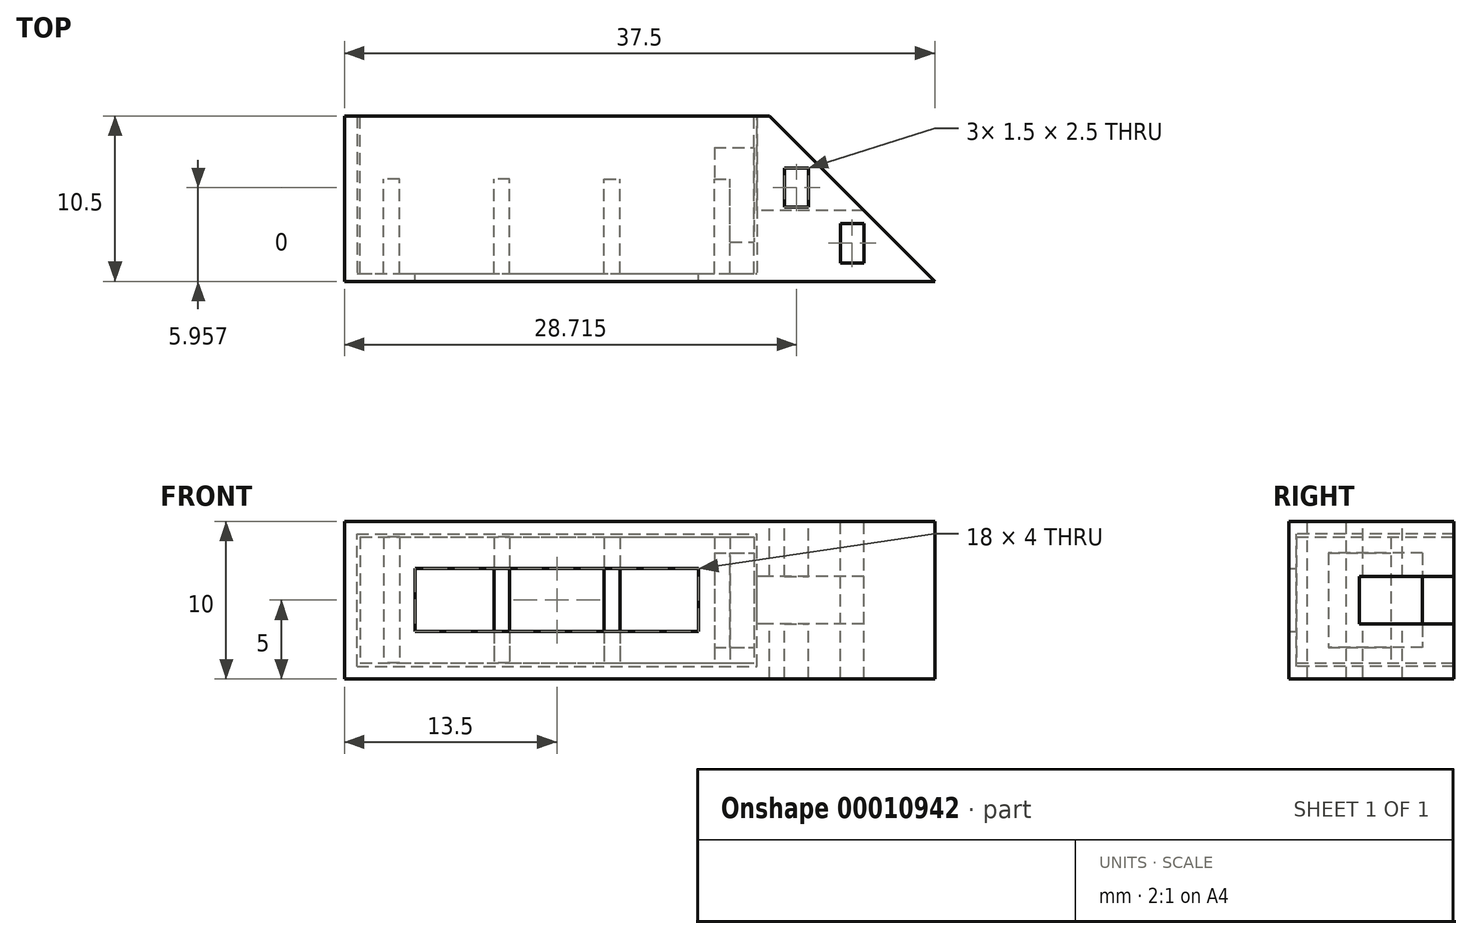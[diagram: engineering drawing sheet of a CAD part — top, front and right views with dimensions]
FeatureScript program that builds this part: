
annotation { "Feature Type Name" : "Feature", "Feature Type Description" : "" }
export const myFeature = defineFeature(function(context is Context, id is Id, definition is map)
    precondition{}
    {
        {
            var Q0;
            Q0=qCreatedBy(makeId("Top.planeOp"),FACE);
            var sketch = newSketch(context, id + "F0", { "sketchPlane" : qUnion([Q0])});
            skLineSegment(sketch, "E0.rect.bottom", {"start": v(-12.5, -5) * mm, "end": v(12.5, -5) * mm});
            skLineSegment(sketch, "E0.rect.top", {"start": v(-12.5, 5) * mm, "end": v(12.5, 5) * mm});
            skLineSegment(sketch, "E0.rect.left", {"start": v(-12.5, -5) * mm, "end": v(-12.5, 5) * mm});
            skLineSegment(sketch, "E0.rect.right", {"start": v(12.5, -5) * mm, "end": v(12.5, 5) * mm});
            skPoint(sketch, "E0.rect.middle", {"position": v(0, 0) * mm});
            skLineSegment(sketch, "E1.bottom", {"start": v(-3, -5) * mm, "end": v(-4, -5) * mm});
            skLineSegment(sketch, "E1.top", {"start": v(-3, 1) * mm, "end": v(-4, 1) * mm});
            skLineSegment(sketch, "E1.left", {"start": v(-3, -5) * mm, "end": v(-3, 1) * mm});
            skLineSegment(sketch, "E1.right", {"start": v(-4, -5) * mm, "end": v(-4, 1) * mm});
            skLineSegment(sketch, "E2.0.MirrorCS", {"start": v(3, -5) * mm, "end": v(3, 1) * mm});
            skLineSegment(sketch, "E3.0.MirrorCS", {"start": v(3, 1) * mm, "end": v(4, 1) * mm});
            skLineSegment(sketch, "E4.0.MirrorCS", {"start": v(4, -5) * mm, "end": v(4, 1) * mm});
            skLineSegment(sketch, "E5", {"start": v(-3.5, 1) * mm, "end": v(-3.5, -6.52) * mm, "construction": true});
            skLineSegment(sketch, "E6.0.MirrorCS", {"start": v(-10, -5) * mm, "end": v(-10, 1) * mm});
            skLineSegment(sketch, "E7.0.MirrorCS", {"start": v(-10, 1) * mm, "end": v(-11, 1) * mm});
            skLineSegment(sketch, "E8.0.MirrorCS", {"start": v(-11, -5) * mm, "end": v(-11, 1) * mm});
            skLineSegment(sketch, "E9", {"start": v(3.5, 1) * mm, "end": v(3.5, -5) * mm, "construction": true});
            skLineSegment(sketch, "E10.0.MirrorCS", {"start": v(11, -5) * mm, "end": v(11, 1) * mm});
            skLineSegment(sketch, "E11.0.MirrorCS", {"start": v(10, -5) * mm, "end": v(10, 1) * mm});
            skLineSegment(sketch, "E12.0.MirrorCS", {"start": v(10, 1) * mm, "end": v(11, 1) * mm});
            skSolve(sketch);
        }
        {
            var Q0;
            Q0=makeQuery(id+"F0.imprint","IMPRINT",FACE,{"disambiguationData":[TD([[makeQuery(id+"F0.imprint","IMPRINT",EDGE,{"derivedFrom":sQuery(id+"F0.wireOp",EDGE,"E0.rect.top")}),-1.0]])]});
            extrude(context, id + "F1", {"entities" : qUnion([Q0]), "depth" : 8 * mm});
        }
        {
            var Q0;
            Q0=makeQuery(id+"F1.opExtrude","SWEPT_FACE",FACE,{"disambiguationData":[OSD([sQuery(id+"F0.wireOp",EDGE,"E0.rect.right")])]});
            var sketch = newSketch(context, id + "F2", { "sketchPlane" : qUnion([Q0])});
            skLineSegment(sketch, "E13", {"start": v(5, 4) * mm, "end": v(-5, 4) * mm, "construction": true});
            skLineSegment(sketch, "E14", {"start": v(0, 8) * mm, "end": v(0, 0) * mm, "construction": true});
            skLineSegment(sketch, "E15.rect.bottom", {"start": v(3, 7) * mm, "end": v(-3, 7) * mm});
            skLineSegment(sketch, "E15.rect.top", {"start": v(3, 1) * mm, "end": v(-3, 1) * mm});
            skLineSegment(sketch, "E15.rect.left", {"start": v(3, 7) * mm, "end": v(3, 1) * mm});
            skLineSegment(sketch, "E15.rect.right", {"start": v(-3, 7) * mm, "end": v(-3, 1) * mm});
            skPoint(sketch, "E15.rect.middle", {"position": v(0, 4) * mm});
            skSolve(sketch);
        }
        {
            var Q0;
            Q0=makeQuery(id+"F2.imprint","IMPRINT",FACE,{"disambiguationData":[TD([[makeQuery(id+"F2.imprint","IMPRINT",EDGE,{"derivedFrom":sQuery(id+"F2.wireOp",EDGE,"E15.rect.bottom")}),1.0]])]});
            extrude(context, id + "F3", {"entities" : qUnion([Q0]), "operationType" : NewBodyOperationType.REMOVE, "oppositeDirection" : true, "depth" : 2.5 * mm});
        }
        {
            var Q0;
            {var subQ0=sQuery(id+"F0.wireOp",EDGE,"E0.rect.bottom");Q0=makeQuery(id+"F1.opExtrude","SWEPT_FACE",FACE,{"disambiguationData":[OSD([subQ0]),TDD([makeQuery(id+"F0.imprint","IMPRINT",EDGE,{"disambiguationData":[TD([[makeQuery(id+"F0.imprint","INTERSECT",VERTEX,{"derivedFrom":[subQ0,sQuery(id+"F0.wireOp",EDGE,"E2.0.MirrorCS")]}),1.0]])],"derivedFrom":subQ0})])]});}
            var sketch = newSketch(context, id + "F4", { "sketchPlane" : qUnion([Q0])});
            skLineSegment(sketch, "E16", {"start": v(0, 0) * mm, "end": v(0, 8) * mm, "construction": true});
            skLineSegment(sketch, "E17", {"start": v(0, 8) * mm, "end": v(0, 4) * mm, "construction": true});
            skLineSegment(sketch, "E18", {"start": v(0, 4) * mm, "end": v(-12.53, 4) * mm, "construction": true});
            skLineSegment(sketch, "E19.rect.bottom", {"start": v(-13.5, -1) * mm, "end": v(13.5, -1) * mm});
            skLineSegment(sketch, "E19.rect.top", {"start": v(-13.5, 9) * mm, "end": v(13.5, 9) * mm});
            skLineSegment(sketch, "E19.rect.left", {"start": v(-13.5, -1) * mm, "end": v(-13.5, 9) * mm});
            skLineSegment(sketch, "E19.rect.right", {"start": v(13.5, -1) * mm, "end": v(13.5, 9) * mm});
            skPoint(sketch, "E19.rect.middle", {"position": v(0, 4) * mm});
            skLineSegment(sketch, "E20.rect.bottom", {"start": v(-9, 2) * mm, "end": v(9, 2) * mm});
            skLineSegment(sketch, "E20.rect.top", {"start": v(-9, 6) * mm, "end": v(9, 6) * mm});
            skLineSegment(sketch, "E20.rect.left", {"start": v(-9, 2) * mm, "end": v(-9, 6) * mm});
            skLineSegment(sketch, "E20.rect.right", {"start": v(9, 2) * mm, "end": v(9, 6) * mm});
            skLineSegment(sketch, "E21.rect.bottom", {"start": v(-12.7, -0.2) * mm, "end": v(12.7, -0.2) * mm});
            skLineSegment(sketch, "E21.rect.top", {"start": v(-12.7, 8.2) * mm, "end": v(12.7, 8.2) * mm});
            skLineSegment(sketch, "E21.rect.left", {"start": v(-12.7, -0.2) * mm, "end": v(-12.7, 8.2) * mm});
            skLineSegment(sketch, "E21.rect.right", {"start": v(12.7, -0.2) * mm, "end": v(12.7, 8.2) * mm});
            skSolve(sketch);
        }
        {
            var Q0;
            Q0 = qSketchRegion(id + "F4", true);
            var Q1;
            {var subQ16=sQuery(id+"F4.wireOp",EDGE,"E20.rect.left");Q1=makeQuery(id+"F4.imprint","IMPRINT",FACE,{"disambiguationData":[TD([[makeQuery(id+"F4.imprint","IMPRINT",EDGE,{"derivedFrom":subQ16}),1.0]])]});}
            var Q2;
            {var subQ0=sQuery(id+"F0.wireOp",EDGE,"E0.rect.bottom");var subQ1=sQuery(id+"F0.wireOp",EDGE,"E2.0.MirrorCS");var subQ7=makeQuery(id+"F1.opExtrude","CAP_EDGE",EDGE,{"disambiguationData":[OSD([subQ0]),TDD([makeQuery(id+"F0.imprint","IMPRINT",EDGE,{"disambiguationData":[TD([[makeQuery(id+"F0.imprint","INTERSECT",VERTEX,{"derivedFrom":[subQ0,subQ1]}),1.0]])],"derivedFrom":subQ0})])],"isStart":false});Q2=makeQuery(id+"F4.imprint","IMPRINT",FACE,{"disambiguationData":[TD([[makeQuery(id+"F4.imprint","IMPRINT",EDGE,{"derivedFrom":subQ7}),-1.0]])]});}
            var Q3;
            {var subQ0=sQuery(id+"F0.wireOp",EDGE,"E0.rect.bottom");var subQ1=sQuery(id+"F0.wireOp",EDGE,"E2.0.MirrorCS");var subQ7=makeQuery(id+"F1.opExtrude","CAP_EDGE",EDGE,{"disambiguationData":[OSD([subQ0]),TDD([makeQuery(id+"F0.imprint","IMPRINT",EDGE,{"disambiguationData":[TD([[makeQuery(id+"F0.imprint","INTERSECT",VERTEX,{"derivedFrom":[subQ0,subQ1]}),1.0]])],"derivedFrom":subQ0})])],"isStart":true});Q3=makeQuery(id+"F4.imprint","IMPRINT",FACE,{"disambiguationData":[TD([[makeQuery(id+"F4.imprint","IMPRINT",EDGE,{"derivedFrom":subQ7}),1.0]])]});}
            extrude(context, id + "F5", {"entities" : qUnion([Q0, Q1, Q2, Q3]), "depth" : .5 * mm});
        }
        {
            var Q0;
            Q0=makeQuery(id+"F4.imprint","IMPRINT",FACE,{"disambiguationData":[TD([[makeQuery(id+"F4.imprint","IMPRINT",EDGE,{"derivedFrom":sQuery(id+"F4.wireOp",EDGE,"E19.rect.bottom")}),1.0]])]});
            extrude(context, id + "F6", {"entities" : qUnion([Q0]), "operationType" : NewBodyOperationType.ADD, "oppositeDirection" : true, "depth" : 10 * mm});
        }
        {
            var Q0;
            {var subQ0=sQuery(id+"F4.wireOp",EDGE,"E19.rect.top");Q0=makeQuery(id+"F6.boolean.opBoolean","MERGE",FACE,{"derivedFrom":[makeQuery(id+"F5.opExtrude","SWEPT_FACE",FACE,{"disambiguationData":[OSD([subQ0])]}),makeQuery(id+"F6.opExtrude","SWEPT_FACE",FACE,{"disambiguationData":[OSD([subQ0])]})]});}
            var sketch = newSketch(context, id + "F7", { "sketchPlane" : qUnion([Q0])});
            skLineSegment(sketch, "E22", {"start": v(13.5, -5.5) * mm, "end": v(24, -5.5) * mm});
            skLineSegment(sketch, "E23", {"start": v(24, -5.5) * mm, "end": v(13.5, 5) * mm});
            skLineSegment(sketch, "E24", {"start": v(13.5, -5.5) * mm, "end": v(18.75, -0.25) * mm, "construction": true});
            skLineSegment(sketch, "E25", {"start": v(17.34, -1.66) * mm, "end": v(18.75, -3.08) * mm, "construction": true});
            skLineSegment(sketch, "E26.rect.bottom", {"start": v(19.5, -4.33) * mm, "end": v(18, -4.33) * mm});
            skLineSegment(sketch, "E26.rect.top", {"start": v(19.5, -1.83) * mm, "end": v(18, -1.83) * mm});
            skLineSegment(sketch, "E26.rect.left", {"start": v(19.5, -4.33) * mm, "end": v(19.5, -1.83) * mm});
            skLineSegment(sketch, "E26.rect.right", {"start": v(18, -4.33) * mm, "end": v(18, -1.83) * mm});
            skPoint(sketch, "E26.rect.middle", {"position": v(18.75, -3.08) * mm});
            skLineSegment(sketch, "E27", {"start": v(17.34, -1.66) * mm, "end": v(15.21, 0.46) * mm, "construction": true});
            skLineSegment(sketch, "E28.rect.bottom", {"start": v(14.46, 1.7) * mm, "end": v(15.96, 1.7) * mm});
            skLineSegment(sketch, "E28.rect.top", {"start": v(14.46, -0.8) * mm, "end": v(15.96, -0.8) * mm});
            skLineSegment(sketch, "E28.rect.left", {"start": v(14.46, 1.7) * mm, "end": v(14.46, -0.8) * mm});
            skLineSegment(sketch, "E28.rect.right", {"start": v(15.96, 1.7) * mm, "end": v(15.96, -0.8) * mm});
            skPoint(sketch, "E28.rect.middle", {"position": v(15.21, 0.46) * mm});
            skSolve(sketch);
        }
        {
            var Q0;
            Q0=makeQuery(id+"F7.imprint","IMPRINT",FACE,{"disambiguationData":[TD([[makeQuery(id+"F7.imprint","IMPRINT",EDGE,{"derivedFrom":sQuery(id+"F7.wireOp",EDGE,"E22")}),1.0]])]});
            var Q1;
            {var subQ0=sQuery(id+"F4.wireOp",EDGE,"E19.rect.bottom");Q1=makeQuery(id+"F6.boolean.opBoolean","MERGE",FACE,{"derivedFrom":[makeQuery(id+"F5.opExtrude","SWEPT_FACE",FACE,{"disambiguationData":[OSD([subQ0])]}),makeQuery(id+"F6.opExtrude","SWEPT_FACE",FACE,{"disambiguationData":[OSD([subQ0])]})]});}
            extrude(context, id + "F8", {"entities" : qUnion([Q0]), "operationType" : NewBodyOperationType.ADD, "endBound" : BoundingType.UP_TO_SURFACE, "oppositeDirection" : true, "endBoundEntityFace" : qUnion([Q1]), "depth" : 25 * mm});
        }
        {
            var Q0;
            Q0=makeQuery(id+"F6.opExtrude","CAP_FACE",FACE,{"disambiguationData":[OSD([sQuery(id+"F4.wireOp",EDGE,"E19.rect.bottom"),sQuery(id+"F4.wireOp",EDGE,"E19.rect.top"),sQuery(id+"F4.wireOp",EDGE,"E19.rect.left"),sQuery(id+"F4.wireOp",EDGE,"E19.rect.right"),sQuery(id+"F4.wireOp",EDGE,"E21.rect.bottom"),sQuery(id+"F4.wireOp",EDGE,"E21.rect.top"),sQuery(id+"F4.wireOp",EDGE,"E21.rect.left"),sQuery(id+"F4.wireOp",EDGE,"E21.rect.right")])],"isStart":false});
            var sketch = newSketch(context, id + "F9", { "sketchPlane" : qUnion([Q0])});
            skLineSegment(sketch, "E29", {"start": v(-13.5, 4) * mm, "end": v(-12.7, 4) * mm, "construction": true});
            skLineSegment(sketch, "E30.rect.bottom", {"start": v(-13.5, 2.5) * mm, "end": v(-12.7, 2.5) * mm});
            skLineSegment(sketch, "E30.rect.top", {"start": v(-13.5, 5.5) * mm, "end": v(-12.7, 5.5) * mm});
            skLineSegment(sketch, "E30.rect.left", {"start": v(-13.5, 2.5) * mm, "end": v(-13.5, 5.5) * mm});
            skLineSegment(sketch, "E30.rect.right", {"start": v(-12.7, 2.5) * mm, "end": v(-12.7, 5.5) * mm});
            skPoint(sketch, "E30.rect.middle", {"position": v(-13.1, 4) * mm});
            skLineSegment(sketch, "E31.bottom", {"start": v(-13.5, 5.5) * mm, "end": v(-25.84, 5.5) * mm});
            skLineSegment(sketch, "E31.top", {"start": v(-13.5, 2.5) * mm, "end": v(-25.84, 2.5) * mm});
            skLineSegment(sketch, "E31.left", {"start": v(-13.5, 5.5) * mm, "end": v(-13.5, 2.5) * mm});
            skLineSegment(sketch, "E31.right", {"start": v(-25.84, 5.5) * mm, "end": v(-25.84, 2.5) * mm});
            skSolve(sketch);
        }
        {
            var Q0;
            Q0=makeQuery(id+"F9.imprint","IMPRINT",FACE,{"disambiguationData":[TD([[makeQuery(id+"F9.imprint","IMPRINT",EDGE,{"derivedFrom":sQuery(id+"F9.wireOp",EDGE,"E30.rect.bottom")}),1.0]])]});
            var Q1;
            Q1=makeQuery(id+"F9.imprint","IMPRINT",FACE,{"disambiguationData":[TD([[makeQuery(id+"F9.imprint","IMPRINT",EDGE,{"derivedFrom":sQuery(id+"F9.wireOp",EDGE,"E31.bottom")}),1.0]])]});
            extrude(context, id + "F10", {"entities" : qUnion([Q0, Q1]), "operationType" : NewBodyOperationType.REMOVE, "oppositeDirection" : true, "depth" : 6 * mm});
        }
    });
